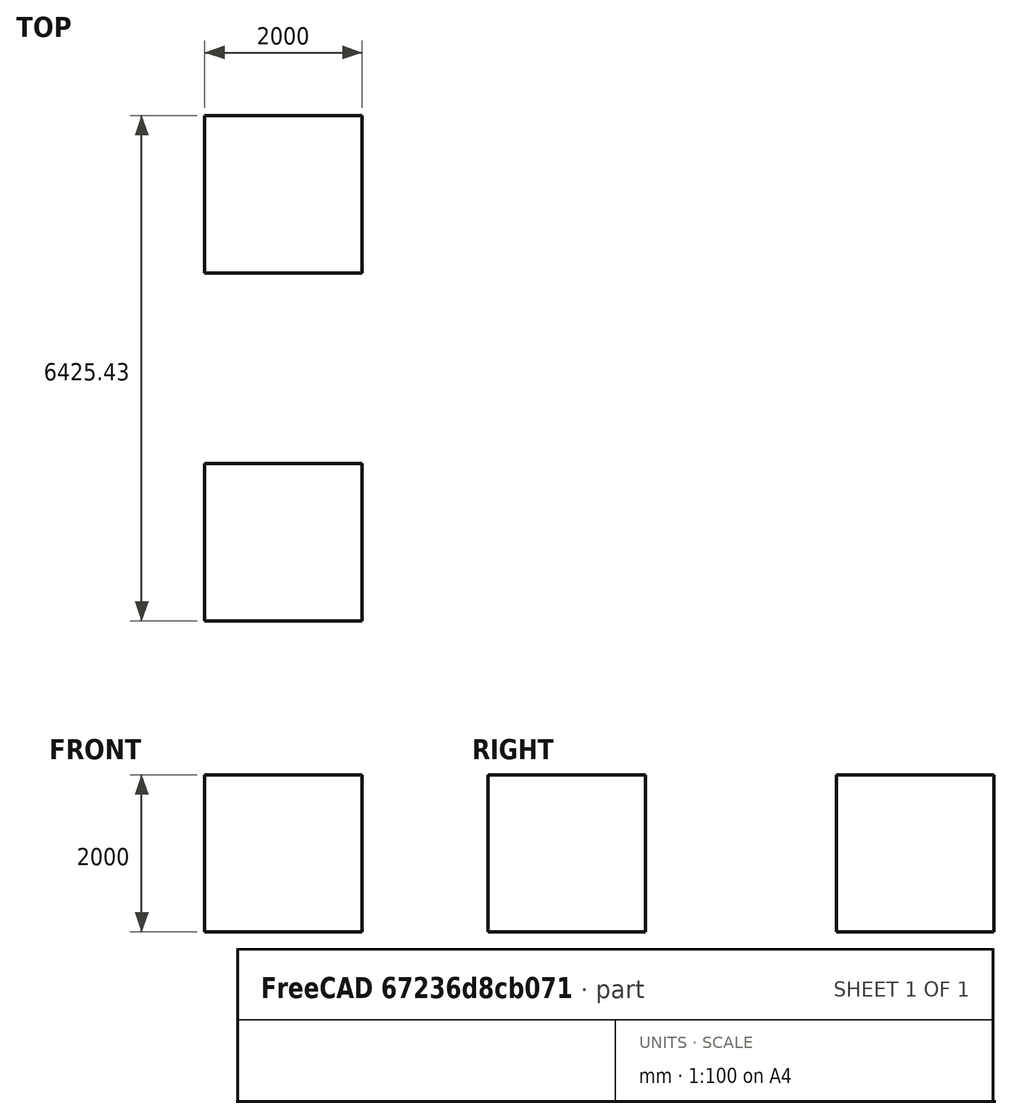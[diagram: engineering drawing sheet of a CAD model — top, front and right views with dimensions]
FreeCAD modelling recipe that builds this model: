
FCSTD DOCUMENT  (FreeCAD 0.19R21310 (Git))
Label: Mapped_Items_03_PASS
License: All rights reserved
LicenseURL: http://en.wikipedia.org/wiki/All_rights_reserved
objects: Part::FeaturePython×2, Part::Part2DObjectPython×1, App::MaterialObjectPython×1, App::DocumentObjectGroupPython×1, App::DocumentObjectGroup×1
note: 3 computed .brp shape members not serialized (recipe doc carries the construction recipe); baked Part::Feature solids carry a one-line shape summary decoded from their .brp

FEATURE [Part::Part2DObjectPython] Rectangle  # Draft 2D object (typed FeaturePython)
  Area = 4e+06
  ChamferSize = 0
  Columns = 1
  FilletRadius = 0
  Height = 2000
  Length = 2000
  MakeFace = true
  Placement = pos=(-1000,-1000,-1000) rot=(0.707107,0.707107,0;3.14159rad)
  Rows = 1
FEATURE [App::MaterialObjectPython] Material  # material (typed FeaturePython)
  Material = Name=Material; Transparency=0
  Transparency = 0
FEATURE [Part::FeaturePython] Wall  label="Cube"  # Arch/BIM 166 (typed FeaturePython)
  Align = 2
  Area = 0
  Base = -> Rectangle
  BlockHeight = 0
  BlockLength = 0
  CountBroken = 0
  CountEntire = 0
  Face = 0
  GlobalId = 08z8rOrVP10hPtOuit9j8u
  Height = 2000
  HorizontalArea = 4e+06
  IfcData = IfcUID=08z8rOrVP10hPtOuit9j8u,+2 more (map truncated)
  IfcType = 166
  Joint = 0
  Length = 0
  MakeBlocks = false
  Material = -> Material
  MoveBase = false
  MoveWithHost = false
  Normal = (0,1.1e-15,1)
  OffsetFirst = 0
  OffsetSecond = 0
  PerimeterLength = 8000
  PredefinedType = 10
  VerticalArea = 1.6e+07
  Width = 150
FEATURE [Part::FeaturePython] Wall001  label="Cube.001"  # Arch/BIM 166 (typed FeaturePython)
  Align = 2
  Area = 0
  BlockHeight = 0
  BlockLength = 0
  CloneOf = -> Wall
  CountBroken = 0
  CountEntire = 0
  Face = 0
  GlobalId = 1b3GiXEVnCRfnIDaERMIl9
  Height = 2000
  HorizontalArea = 4e+06
  IfcData = IfcUID=1b3GiXEVnCRfnIDaERMIl9,+2 more (map truncated)
  IfcType = 166
  Joint = 0
  Length = 0
  MakeBlocks = false
  Material = -> Material
  MoveBase = false
  MoveWithHost = false
  Normal = (0,0,0)
  OffsetFirst = 0
  OffsetSecond = 0
  PerimeterLength = 8000
  Placement = pos=(2.7e-14,4425.43,3.967e-12) rot=(0,0,1;0rad)
  PredefinedType = 10
  VerticalArea = 1.6e+07
  Width = 150
FEATURE [App::DocumentObjectGroupPython] MaterialContainer  label="Materials"  # scripted group (container) (typed FeaturePython)
  Group = -> [Material]
FEATURE [App::DocumentObjectGroup] Group  label="Mapped_Items_02_PASS.ifc"
  Group = -> [Wall001,Wall]
